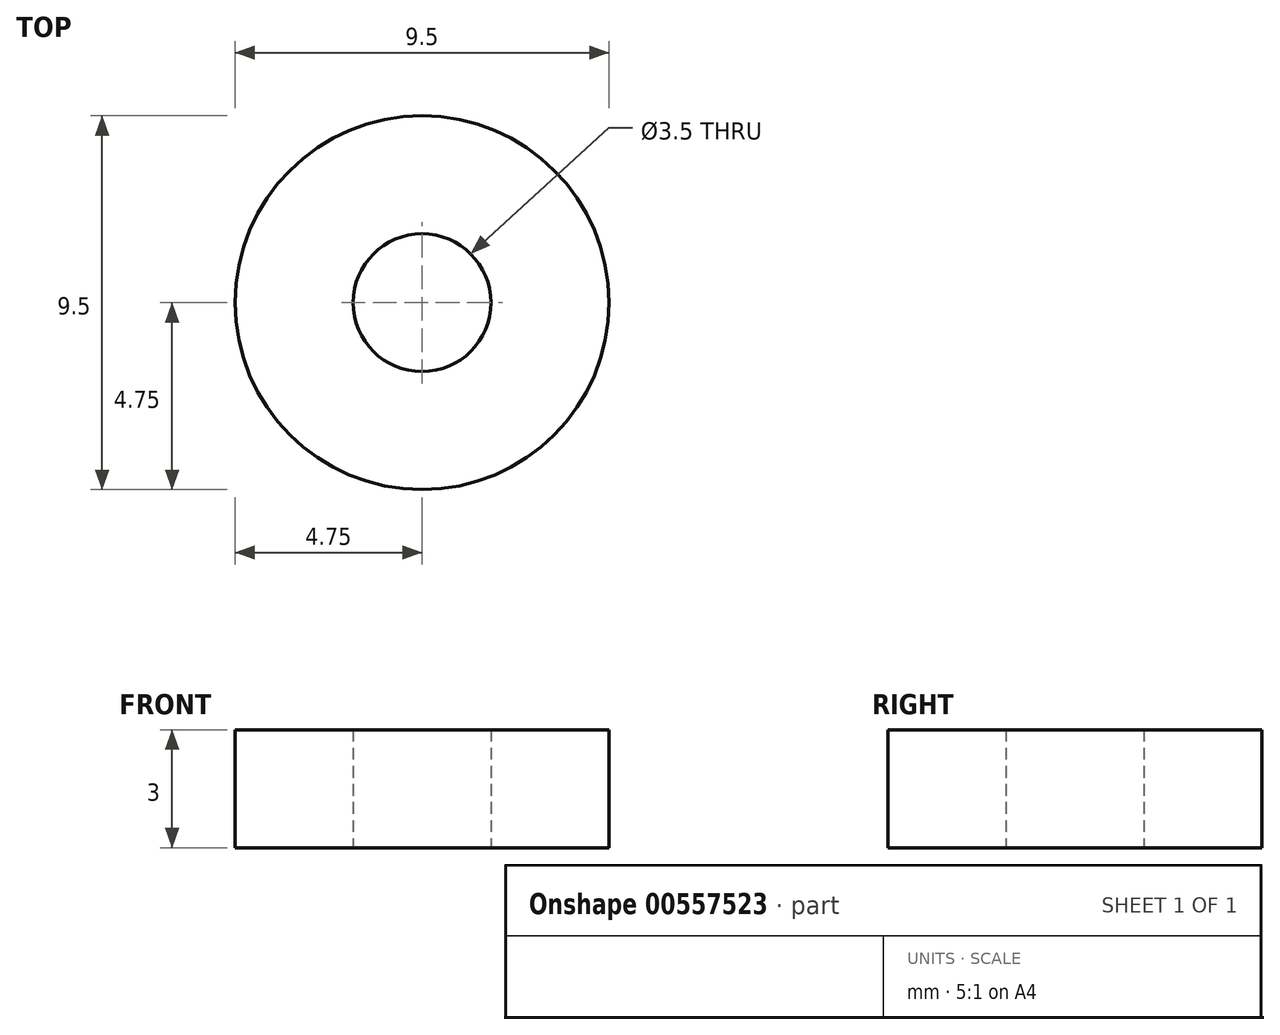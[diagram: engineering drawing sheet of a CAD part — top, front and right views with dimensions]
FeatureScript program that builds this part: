
annotation { "Feature Type Name" : "Feature", "Feature Type Description" : "" }
export const myFeature = defineFeature(function(context is Context, id is Id, definition is map)
    precondition{}
    {
        {
            var Q0;
            Q0=qCreatedBy(makeId("Top.planeOp"),FACE);
            var sketch = newSketch(context, id + "F0", { "sketchPlane" : qUnion([Q0])});
            skCircle(sketch, "E0", {"center": v(0, 0) * mm, "radius": 1.75 * mm});
            skCircle(sketch, "E1.0", {"center": v(0, 0) * mm, "radius": 4.75 * mm});
            skSolve(sketch);
        }
        {
            var Q0;
            Q0=qSketchRegion(id+"F0",true);
            extrude(context, id + "F1", {"entities" : qUnion([Q0]), "depth" : 3 * mm, "offsetDistance" : 25 * mm});
        }
    });
